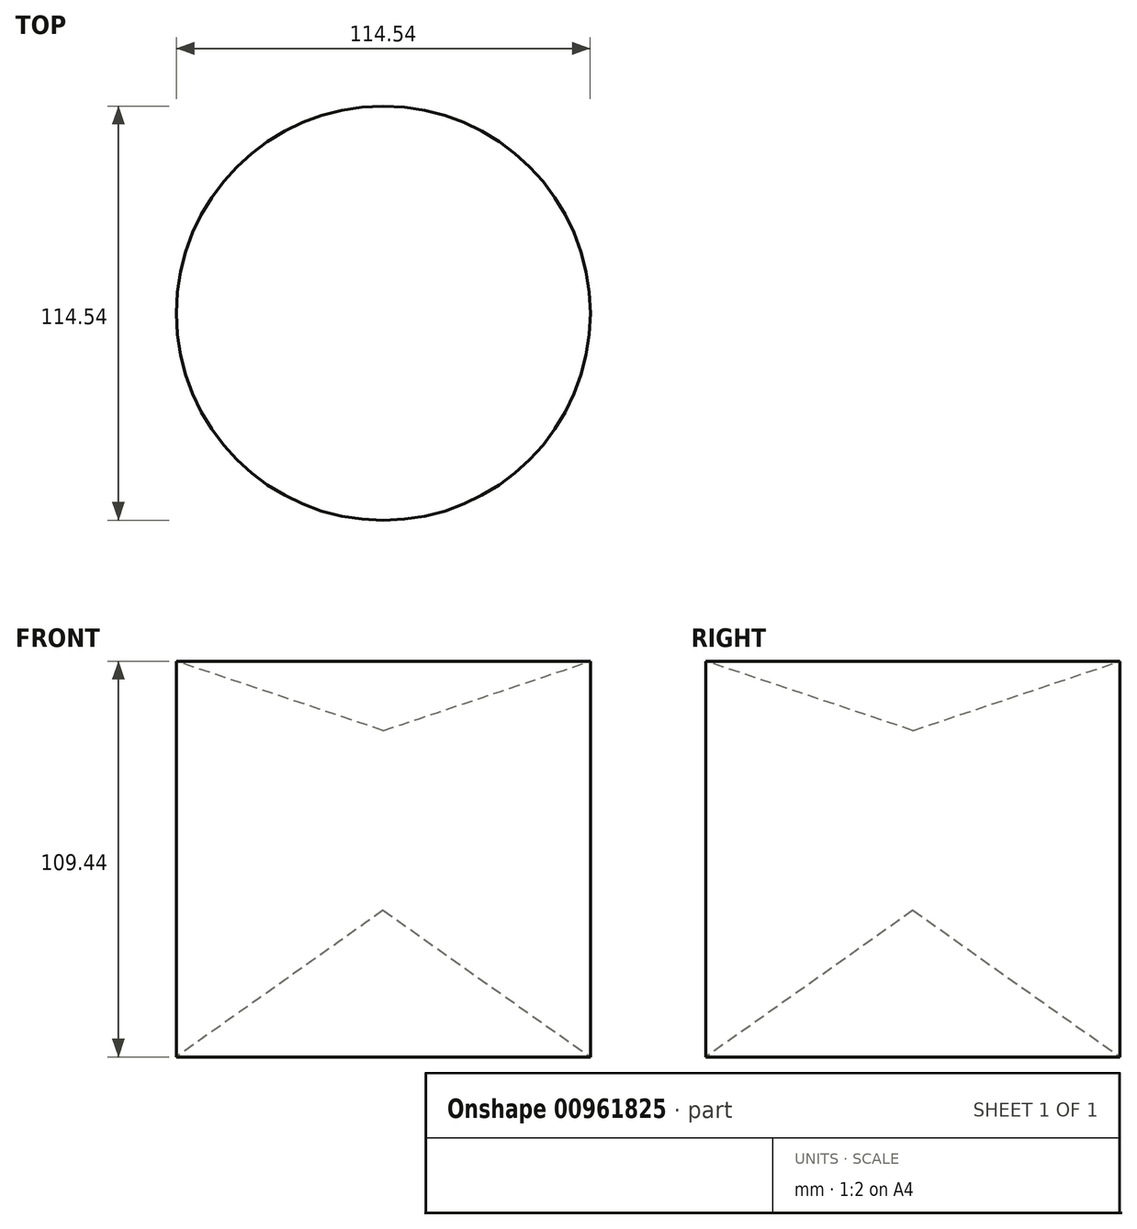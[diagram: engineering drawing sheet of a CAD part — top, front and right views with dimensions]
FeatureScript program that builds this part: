
annotation { "Feature Type Name" : "Feature", "Feature Type Description" : "" }
export const myFeature = defineFeature(function(context is Context, id is Id, definition is map)
    precondition{}
    {
        {
            var Q0;
            Q0=qCreatedBy(makeId("Front.planeOp"),FACE);
            var sketch = newSketch(context, id + "F0", { "sketchPlane" : qUnion([Q0])});
            skLineSegment(sketch, "E0", {"start": v(0, 0) * mm, "end": v(0, 49.72) * mm});
            skLineSegment(sketch, "E1", {"start": v(0, 49.72) * mm, "end": v(57.27, 68.91) * mm});
            skLineSegment(sketch, "E2", {"start": v(57.27, 68.91) * mm, "end": v(57.27, -40.53) * mm});
            skLineSegment(sketch, "E3", {"start": v(57.27, -40.53) * mm, "end": v(0, 0) * mm});
            skSolve(sketch);
        }
        {
            var Q0;
            Q0=makeQuery(id+"F0.imprint","IMPRINT",FACE,{"disambiguationData":[TD([[makeQuery(id+"F0.imprint","IMPRINT",EDGE,{"derivedFrom":sQuery(id+"F0.wireOp",EDGE,"E0")}),-1.0]])]});
            var Q1;
            Q1=sQuery(id+"F0.wireOp",EDGE,"E0");
            revolve(context, id + "F1", {"surfaceOperationType" : NewSurfaceOperationType.NEW, "entities" : qUnion([Q0]), "axis" : qUnion([Q1]), "revolveType" : RevolveType.FULL});
        }
    });
